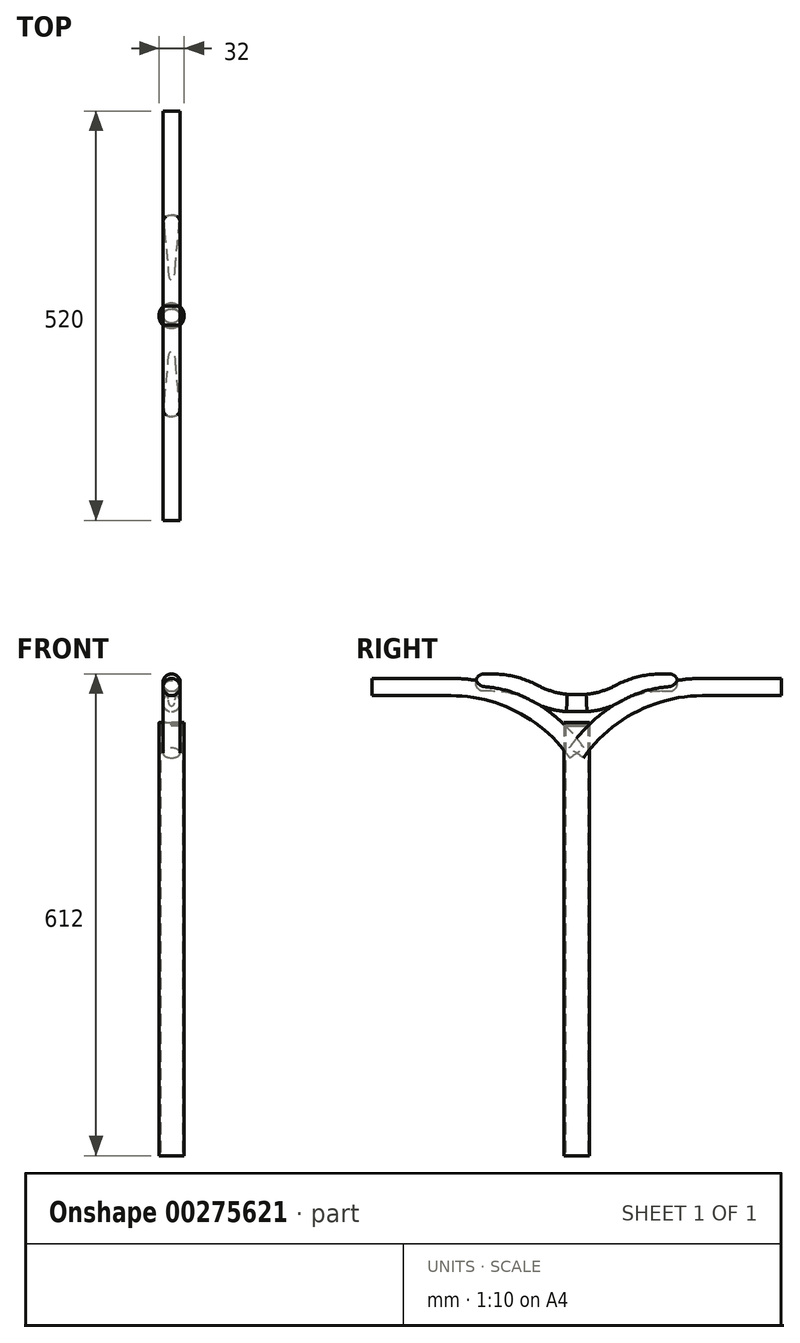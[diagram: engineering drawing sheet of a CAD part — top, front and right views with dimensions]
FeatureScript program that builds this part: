
annotation { "Feature Type Name" : "Feature", "Feature Type Description" : "" }
export const myFeature = defineFeature(function(context is Context, id is Id, definition is map)
    precondition{}
    {
        {
            var Q0;
            Q0=qCreatedBy(makeId("Top.planeOp"),FACE);
            var sketch = newSketch(context, id + "F0", { "sketchPlane" : qUnion([Q0])});
            skCircle(sketch, "E0", {"center": v(0, 0) * mm, "radius": 16 * mm});
            skSolve(sketch);
        }
        {
            var Q0;
            Q0=qSketchRegion(id+"F0",true);
            extrude(context, id + "F1", {"entities" : qUnion([Q0]), "depth" : 550 * mm});
        }
        {
            var Q0;
            Q0=qCreatedBy(makeId("Right.planeOp"),FACE);
            var sketch = newSketch(context, id + "F2", { "sketchPlane" : qUnion([Q0])});
            skArc(sketch, "E1", {"start": v(160, 595) * mm, "mid": v(69.75, 572.86) * mm, "end": v(0, 511.47) * mm});
            skLineSegment(sketch, "E2", {"start": v(160, 595) * mm, "end": v(260, 595) * mm});
            skSolve(sketch);
        }
        {
            var Q0;
            Q0=sQuery(id+"F2.wireOp",VERTEX,"E2.end");
            var Q1;
            Q1=qCreatedBy(makeId("Front.planeOp"),FACE);
            cPlane(context, id + "F3", {"entities" : qUnion([Q0, Q1]), "cplaneType" : CPlaneType.PLANE_POINT, "offset" : 25 * mm, "width" : 150 * mm, "height" : 150 * mm});
        }
        {
            var Q0;
            Q0=qCreatedBy(id+"F3.planeOp",FACE);
            var sketch = newSketch(context, id + "F4", { "sketchPlane" : qUnion([Q0])});
            skCircle(sketch, "E3", {"center": v(0, 220.01) * mm, "radius": 11 * mm});
            skCircle(sketch, "E4", {"center": v(0, 595.31) * mm, "radius": 11 * mm});
            skSolve(sketch);
        }
        {
            var Q0;
            Q0=makeQuery(id+"F4.imprint","IMPRINT",FACE,{"disambiguationData":[TD([[makeQuery(id+"F4.imprint","IMPRINT",EDGE,{"derivedFrom":sQuery(id+"F4.wireOp",EDGE,"E4")}),1.0]])]});
            var Q1;
            Q1=sQuery(id+"F2.wireOp",EDGE,"E2");
            var Q2;
            Q2=sQuery(id+"F2.wireOp",EDGE,"E1");
            sweep(context, id + "F5", {"profiles" : qUnion([Q0]), "path" : qUnion([Q1, Q2])});
        }
        {
            var Q0;
            Q0=qCreatedBy(makeId("Right.planeOp"),FACE);
            var sketch = newSketch(context, id + "F6", { "sketchPlane" : qUnion([Q0])});
            skLineSegment(sketch, "E5", {"start": v(-128, 601) * mm, "end": v(-108, 601) * mm});
            skArc(sketch, "E6", {"start": v(-54.42, 587.63) * mm, "mid": v(-80.39, 597.6) * mm, "end": v(-108, 601) * mm});
            skArc(sketch, "E7", {"start": v(-54.42, 587.63) * mm, "mid": v(-34.08, 579.24) * mm, "end": v(-12.5, 575) * mm});
            skLineSegment(sketch, "E8", {"start": v(-12.5, 575) * mm, "end": v(0, 575) * mm});
            skLineSegment(sketch, "E9.MirrorCS", {"start": v(12.5, 575) * mm, "end": v(0, 575) * mm});
            skArc(sketch, "E10.MirrorCS", {"start": v(54.42, 587.63) * mm, "mid": v(34.08, 579.24) * mm, "end": v(12.5, 575) * mm});
            skArc(sketch, "E11.MirrorCS", {"start": v(54.42, 587.63) * mm, "mid": v(80.39, 597.6) * mm, "end": v(108, 601) * mm});
            skLineSegment(sketch, "E12.MirrorCS", {"start": v(128, 601) * mm, "end": v(108, 601) * mm});
            skSolve(sketch);
        }
        {
            var Q0;
            Q0=sQuery(id+"F6.wireOp",VERTEX,"E12.MirrorCS.start");
            var Q1;
            Q1=qCreatedBy(makeId("Front.planeOp"),FACE);
            cPlane(context, id + "F7", {"entities" : qUnion([Q0, Q1]), "cplaneType" : CPlaneType.PLANE_POINT, "offset" : 25 * mm, "width" : 150 * mm, "height" : 150 * mm});
        }
        {
            var Q0;
            Q0=qCreatedBy(id+"F7.planeOp",FACE);
            var sketch = newSketch(context, id + "F8", { "sketchPlane" : qUnion([Q0])});
            skCircle(sketch, "E13", {"center": v(0, 601) * mm, "radius": 11 * mm});
            skSolve(sketch);
        }
        {
            var Q0;
            Q0=makeQuery(id+"F8.imprint","IMPRINT",FACE,{"disambiguationData":[TD([[makeQuery(id+"F8.imprint","IMPRINT",EDGE,{"derivedFrom":sQuery(id+"F8.wireOp",EDGE,"E13")}),1.0]])]});
            var Q1;
            Q1=sQuery(id+"F6.wireOp",EDGE,"E11.MirrorCS");
            var Q2;
            Q2=sQuery(id+"F6.wireOp",EDGE,"E10.MirrorCS");
            var Q3;
            Q3=sQuery(id+"F6.wireOp",EDGE,"E9.MirrorCS");
            var Q4;
            Q4=sQuery(id+"F6.wireOp",EDGE,"E8");
            var Q5;
            Q5=sQuery(id+"F6.wireOp",EDGE,"E7");
            var Q6;
            Q6=sQuery(id+"F6.wireOp",EDGE,"E6");
            var Q7;
            Q7=sQuery(id+"F6.wireOp",EDGE,"E5");
            var Q8;
            Q8=sQuery(id+"F6.wireOp",EDGE,"E12.MirrorCS");
            sweep(context, id + "F9", {"operationType" : NewBodyOperationType.ADD, "profiles" : qUnion([Q0]), "path" : qUnion([Q1, Q2, Q3, Q4, Q5, Q6, Q7, Q8])});
        }
        {
            var Q0;
            Q0=makeQuery(id+"F9.opSweep","CAP_EDGE",EDGE,{"disambiguationData":[OSD([sQuery(id+"F6.wireOp",VERTEX,"E12.MirrorCS.start"),sQuery(id+"F8.wireOp",EDGE,"E13")])],"isStart":true});
            var Q1;
            Q1=makeQuery(id+"F9.opSweep","CAP_EDGE",EDGE,{"disambiguationData":[OSD([sQuery(id+"F6.wireOp",VERTEX,"E5.start"),sQuery(id+"F8.wireOp",EDGE,"E13")])],"isStart":false});
            fillet(context, id + "F10", {"entities" : qUnion([Q0, Q1]), "radius" : 10 * mm, "tangentPropagation" : true, "allowEdgeOverflow" : false});
        }
        {
            var Q0;
            Q0=makeQuery(id+"F5.opSweep","SWEPT_BODY",BODY,{"disambiguationData":[OSD([sQuery(id+"F2.wireOp",EDGE,"E1"),sQuery(id+"F4.wireOp",EDGE,"E4")])]});
            var Q1;
            Q1=qCreatedBy(makeId("Front.planeOp"),FACE);
            mirror(context, id + "F11", {"entities" : qUnion([Q0]), "mirrorPlane" : qUnion([Q1])});
        }
        {
            var Q0;
            Q0=makeQuery(id+"F1.opExtrude","CAP_FACE",FACE,{"disambiguationData":[OSD([sQuery(id+"F0.wireOp",EDGE,"E0")])],"isStart":true});
            shell(context, id + "F12", {"entities" : qUnion([Q0]), "thickness" : 2 * mm});
        }
        {
            var Q0;
            Q0=qCreatedBy(makeId("Right.planeOp"),FACE);
            var sketch = newSketch(context, id + "F13", { "sketchPlane" : qUnion([Q0])});
            skArc(sketch, "E14", {"start": v(-20, 563) * mm, "mid": v(-14.14, 548.86) * mm, "end": v(0, 543) * mm});
            skLineSegment(sketch, "E15", {"start": v(-20, 563) * mm, "end": v(0, 563) * mm});
            skLineSegment(sketch, "E16", {"start": v(0, 543) * mm, "end": v(0, 563) * mm});
            skSolve(sketch);
        }
        {
            var Q0;
            Q0=qSketchRegion(id+"F13",true);
            var Q1;
            Q1=sQuery(id+"F13.wireOp",EDGE,"E16");
            revolve(context, id + "F14", {"operationType" : NewBodyOperationType.REMOVE, "entities" : qUnion([Q0]), "axis" : qUnion([Q1]), "revolveType" : RevolveType.FULL});
        }
        {
            var Q0;
            Q0=makeQuery(id+"F1.opExtrude","CAP_FACE",FACE,{"disambiguationData":[OSD([sQuery(id+"F0.wireOp",EDGE,"E0")])],"isStart":false});
            cPlane(context, id + "F15", {"entities" : qUnion([Q0]), "cplaneType" : CPlaneType.OFFSET, "offset" : 2 * mm, "oppositeDirection" : true, "width" : 150 * mm, "height" : 150 * mm});
        }
        {
            var Q0;
            Q0=qCreatedBy(id+"F15.planeOp",FACE);
            var sketch = newSketch(context, id + "F16", { "sketchPlane" : qUnion([Q0])});
            skCircle(sketch, "E17", {"center": v(0, 0) * mm, "radius": 14 * mm});
            skSolve(sketch);
        }
        {
            var Q0;
            Q0=qSketchRegion(id+"F16",true);
            extrude(context, id + "F17", {"entities" : qUnion([Q0]), "oppositeDirection" : true, "depth" : 2 * mm});
        }
    });
